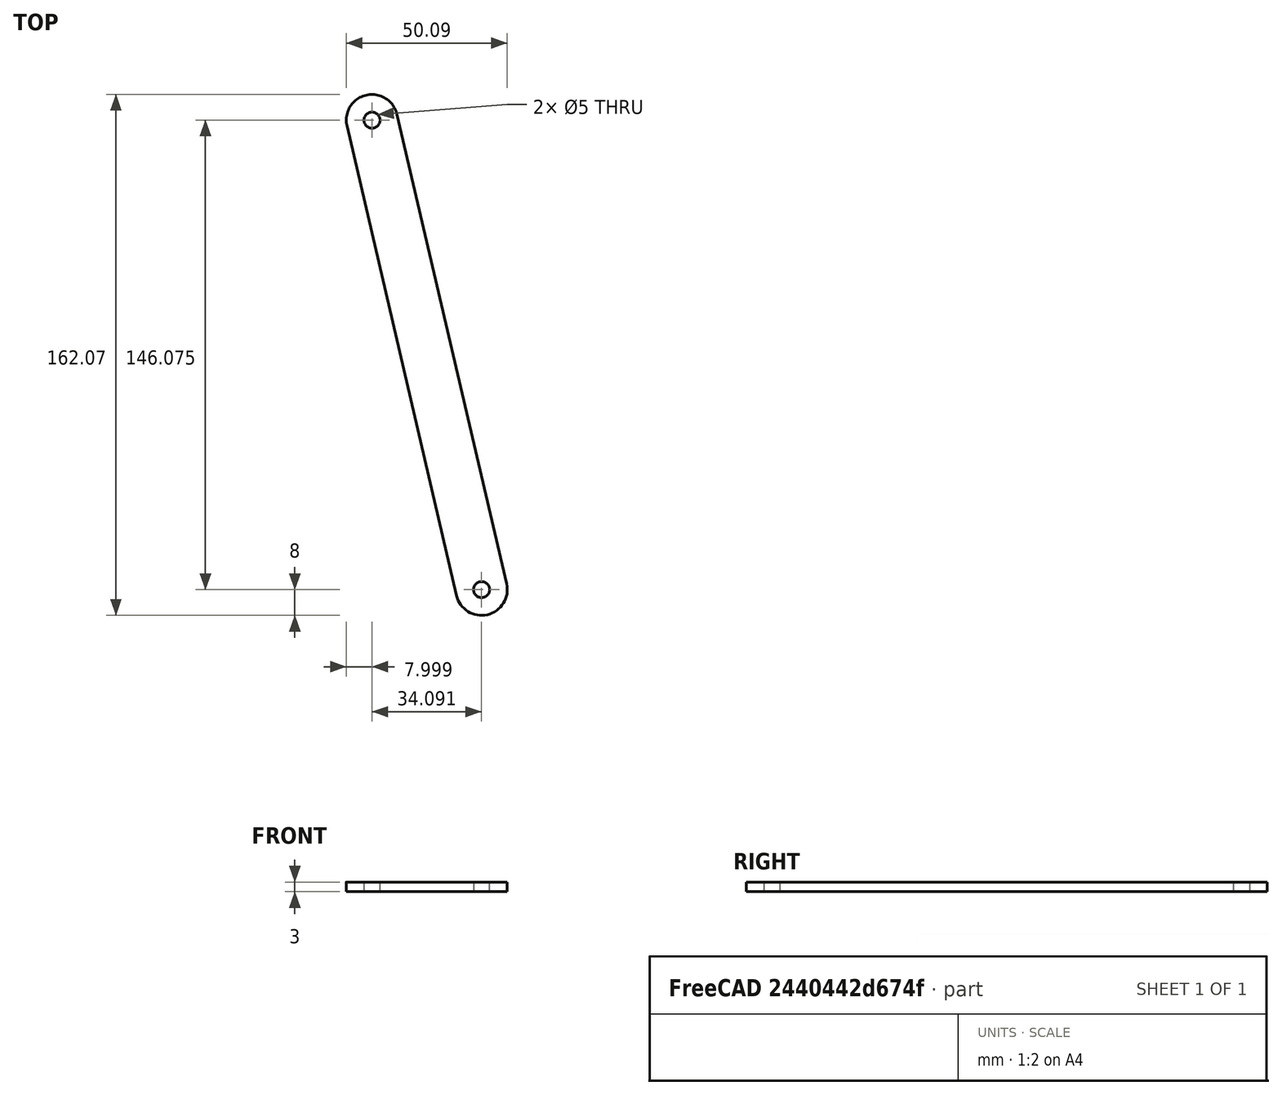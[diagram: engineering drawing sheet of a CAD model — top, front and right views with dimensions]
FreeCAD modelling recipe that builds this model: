
FCSTD DOCUMENT  (FreeCAD 0.19R24276 (Git))
Label: Shatun
License: All rights reserved
LicenseURL: http://en.wikipedia.org/wiki/All_rights_reserved
objects: Sketcher::SketchObject×1, PartDesign::Pad×1, PartDesign::Body×1
note: 4 computed .brp shape members not serialized (recipe doc carries the construction recipe); baked Part::Feature solids carry a one-line shape summary decoded from their .brp

FEATURE [Sketcher::SketchObject] Sketch
  FullyConstrained = false
  MapMode = 5
  Support = -> [XY_Plane]
  sketch-geometry (6):
    g0: ArcOfCircle CenterX=0 CenterY=0 CenterZ=0 NormalX=0 NormalY=0 NormalZ=1 AngleXU=0 Radius=8 StartAngle=3.37087 EndAngle=6.51246
    g1: ArcOfCircle CenterX=-34.091 CenterY=146.075 CenterZ=0 NormalX=0 NormalY=0 NormalZ=1 AngleXU=0 Radius=8 StartAngle=0.229277 EndAngle=3.37087
    g2: LineSegment StartX=7.79065 StartY=1.81819 StartZ=0 EndX=-26.3003 EndY=147.893 EndZ=0
    g3: LineSegment StartX=-7.79065 StartY=-1.81819 StartZ=0 EndX=-41.8816 EndY=144.256 EndZ=0
    g4: Circle CenterX=0 CenterY=0 CenterZ=0 NormalX=0 NormalY=0 NormalZ=1 AngleXU=0 Radius=2.5
    g5: Circle CenterX=-34.091 CenterY=146.075 CenterZ=0 NormalX=0 NormalY=0 NormalZ=1 AngleXU=0 Radius=2.5
  constraints (12):
    c: Tangent(g0,g3) = 1.5708
    c: Tangent(g0,g2) = -1.5708
    c: Tangent(g2,g1) = -1.5708
    c: Tangent(g3,g1) = 1.5708
    c: Equal(g0,g1)
    c: Coincident(g4,g0)
    c: Coincident(g5,g1)
    c: Equal(g4,g5)
    c: Diameter(g5) = 5
    c: Radius(g0) = 8
    c: Coincident(g0,g-1)
    c: Distance(g1,g0) = 150
FEATURE [PartDesign::Pad] Pad
  Direction = (1,1,1)
  Length = 3
  Length2 = 100
  Profile = -> Sketch
  Type = 0
FEATURE [PartDesign::Body] Body  label="Body_Shatun"
  Group = -> [Sketch,Pad]
  Origin = -> Origin
  Tip = -> Pad
